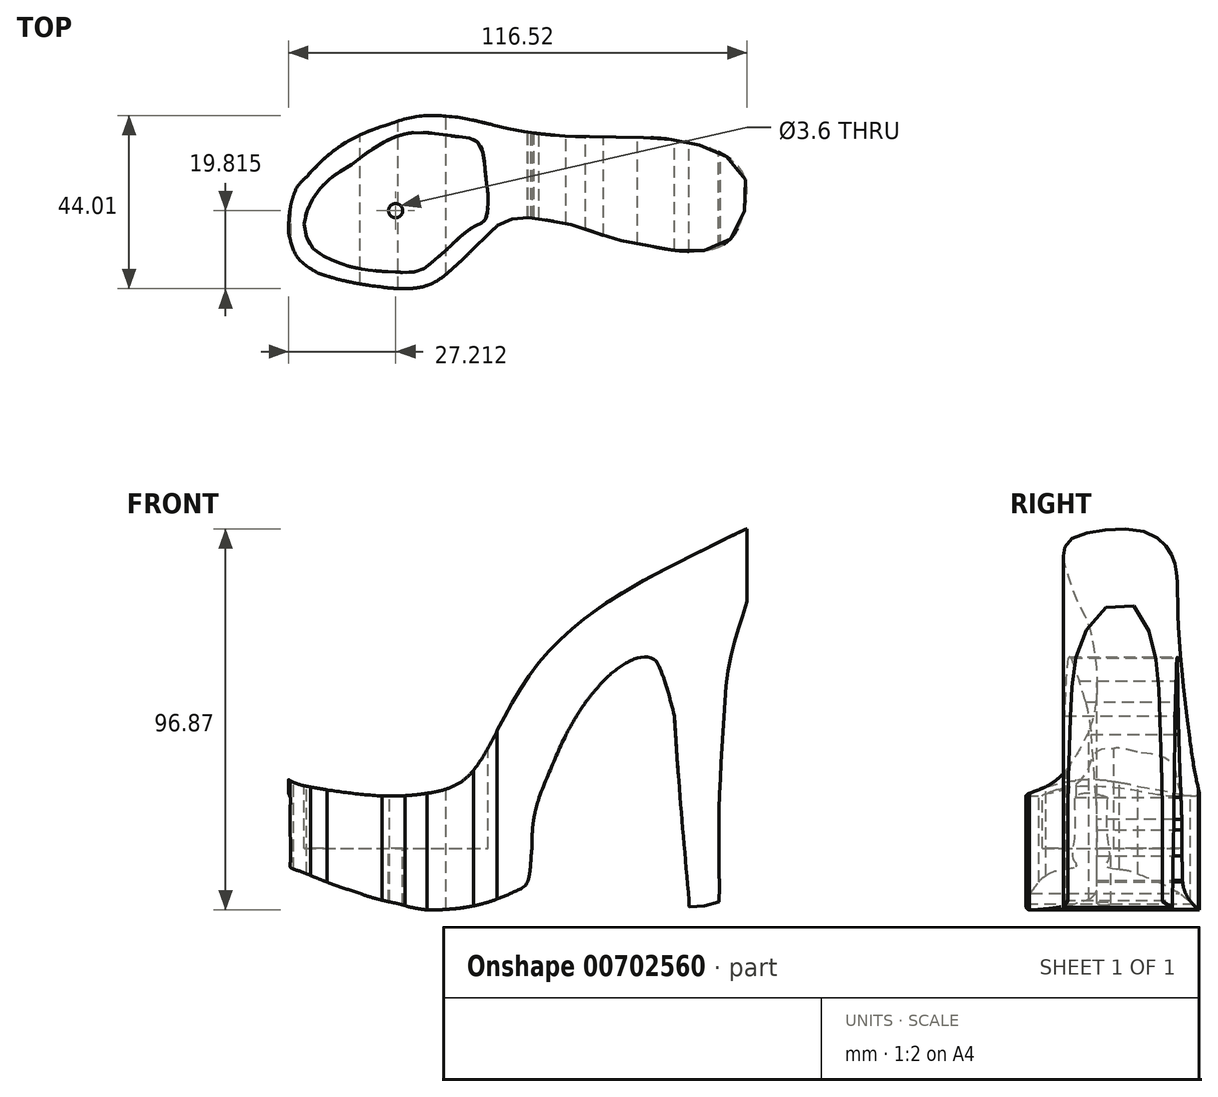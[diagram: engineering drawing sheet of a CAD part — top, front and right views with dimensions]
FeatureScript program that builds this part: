
annotation { "Feature Type Name" : "Feature", "Feature Type Description" : "" }
export const myFeature = defineFeature(function(context is Context, id is Id, definition is map)
    precondition{}
    {
        {
            var Q0;
            Q0=qCreatedBy(makeId("Front.planeOp"),FACE);
            var sketch = newSketch(context, id + "F0", { "sketchPlane" : qUnion([Q0])});
            skFitSpline(sketch, "E0", {"points": [v(-57.93, -19.47) * mm, v(-55.3, -20.89) * mm, v(-50.02, -22.51) * mm, v(-39.07, -24.13) * mm, v(-27.3, -24.74) * mm, v(-16.76, -23.32) * mm, v(-13.11, -21.9) * mm, v(-9.87, -19.47) * mm, v(-6.01, -14.2) * mm, v(-3.78, -10.14) * mm, v(1.7, 0) * mm, v(7.57, 8.72) * mm, v(18.12, 19.27) * mm, v(34.14, 29.81) * mm, v(49.96, 37.93) * mm, v(63.55, 44.21) * mm, v(66.6, 44.42) * mm, v(64.97, 39.75) * mm, v(61.93, 28.6) * mm, v(56.66, 11.15) * mm, v(54.83, -4.66) * mm, v(53.61, -29.2) * mm, v(53.82, -48.27) * mm, v(53.61, -51.51) * mm, v(51.38, -52.53) * mm, v(47.33, -52.93) * mm, v(46.1, -52.93) * mm, v(46.1, -49.69) * mm, v(46.1, -43.4) * mm, v(45.3, -26.97) * mm, v(44.28, -15.62) * mm, v(42.26, -4.46) * mm, v(38.2, 8.52) * mm, v(36.37, 10.34) * mm, v(32.93, 10.34) * mm, v(28.26, 8.52) * mm, v(24.2, 4.46) * mm, v(17.3, -4.46) * mm, v(10, -19.88) * mm, v(6.36, -31.84) * mm, v(4.94, -46.65) * mm, v(2.5, -48.68) * mm, v(-3.17, -51.1) * mm, v(-15.75, -53.54) * mm, v(-27.92, -52.12) * mm, v(-37.65, -49.49) * mm, v(-45.56, -45.23) * mm, v(-51.24, -41.17) * mm, v(-53.07, -35.7) * mm, v(-55.3, -25.15) * mm, v(-57.93, -19.47) * mm]});
            skFitSpline(sketch, "E1", {"points": [v(-55.3, -20.89) * mm, v(-55.3, -25.15) * mm, v(-55.3, -35.7) * mm, v(-55.3, -41.53) * mm, v(-55.3, -42.87) * mm, v(-53.07, -43.82) * mm, v(-49.74, -45.16) * mm, v(-37.65, -49.49) * mm, v(-27.92, -52.12) * mm, v(-15.75, -53.54) * mm, v(4.94, -46.65) * mm, v(4.94, -45.23) * mm, v(5.86, -40.03) * mm, v(6.2, -33.38) * mm, v(7.91, -25.15) * mm, v(14.75, -9.15) * mm, v(24.2, 4.46) * mm, v(32.93, 10.34) * mm, v(38.2, 10.34) * mm, v(41.15, 6.2) * mm, v(42.26, -4.46) * mm, v(46.1, -52.93) * mm], "startDerivative": vector(0.48, -111.33) * mm, "endDerivative": vector(44.54, -510.04) * mm});
            skSolve(sketch);
        }
        {
            var Q0;
            Q0 = qSketchRegion(id + "F0", true);
            extrude(context, id + "F1", {"entities" : qUnion([Q0]), "endBound" : BoundingType.SYMMETRIC, "depth" : 50.8 * mm, "offsetDistance" : 25.4 * mm});
        }
        {
            var Q0;
            Q0=qCreatedBy(makeId("Top.planeOp"),FACE);
            var sketch = newSketch(context, id + "F2", { "sketchPlane" : qUnion([Q0])});
            skFitSpline(sketch, "E2", {"points": [v(-54.46, -12.17) * mm, v(-55.47, -10.75) * mm, v(-55.67, -6.29) * mm, v(-54.46, 0) * mm, v(-51.21, 4.66) * mm, v(-43.1, 12.17) * mm, v(-30.12, 18.05) * mm, v(-15.72, 20.08) * mm, v(-3.75, 17.85) * mm, v(8.21, 15.62) * mm, v(24.24, 14.8) * mm, v(39.65, 14.4) * mm, v(52.22, 11.56) * mm, v(59.12, 6.5) * mm, v(60.74, 0) * mm, v(58.71, -7.7) * mm, v(54.25, -12.78) * mm, v(44.72, -14.2) * mm, v(35.4, -12.78) * mm, v(26.47, -10.95) * mm, v(17.75, -7.9) * mm, v(10.85, -6.5) * mm, v(3.55, -5.68) * mm, v(-2.74, -7.7) * mm, v(-8.82, -13.59) * mm, v(-14.1, -18.66) * mm, v(-20.59, -22.92) * mm, v(-31.94, -23.32) * mm, v(-42.08, -21.3) * mm, v(-50.6, -18.25) * mm, v(-54.46, -12.17) * mm]});
            skLineSegment(sketch, "E3.bottom", {"start": v(-58.72, 26.07) * mm, "end": v(67.31, 26.07) * mm});
            skLineSegment(sketch, "E3.top", {"start": v(-58.72, -26.26) * mm, "end": v(67.31, -26.26) * mm});
            skLineSegment(sketch, "E3.left", {"start": v(-58.72, 26.07) * mm, "end": v(-58.72, -26.26) * mm});
            skLineSegment(sketch, "E3.right", {"start": v(67.31, 26.07) * mm, "end": v(67.31, -26.26) * mm});
            skFitSpline(sketch, "E4", {"points": [v(-2.74, -7.7) * mm, v(-8.82, -13.59) * mm, v(-14.1, -18.66) * mm, v(-20.59, -22.92) * mm, v(-31.94, -23.32) * mm, v(-50.12, -18.66) * mm, v(-55.35, -11.06) * mm, v(-54.46, 0) * mm, v(-51.21, 4.66) * mm, v(-30.12, 18.05) * mm, v(-15.72, 20.08) * mm, v(-3.75, 17.85) * mm], "startDerivative": vector(-79.74, -76.49) * mm, "endDerivative": vector(127.32, -29.11) * mm});
            skSolve(sketch);
        }
        {
            var Q0;
            Q0 = qSketchRegion(id + "F2", true);
            extrude(context, id + "F3", {"entities" : qUnion([Q0]), "operationType" : NewBodyOperationType.REMOVE, "endBound" : BoundingType.SYMMETRIC, "oppositeDirection" : true, "depth" : 127 * mm, "offsetDistance" : 25.4 * mm});
        }
        {
            var Q0;
            Q0=qCreatedBy(makeId("Top.planeOp"),FACE);
            var sketch = newSketch(context, id + "F4", { "sketchPlane" : qUnion([Q0])});
            skFitSpline(sketch, "E5", {"points": [v(-46.27, 3.3) * mm, v(-40.75, 7.22) * mm, v(-31.93, 13.3) * mm, v(-22.95, 15.98) * mm, v(-13.5, 14.98) * mm, v(-7.43, 13.23) * mm, v(-5.64, 4.55) * mm, v(-5.61, -3.12) * mm, v(-12.03, -7.96) * mm, v(-18.45, -12.8) * mm, v(-22.52, -16.22) * mm, v(-30.24, -17.87) * mm, v(-39.14, -17.29) * mm, v(-46.84, -15.5) * mm, v(-50.32, -12.45) * mm, v(-51.6, -5.81) * mm, v(-46.27, 3.3) * mm]});
            skFitSpline(sketch, "E6", {"points": [v(-46.84, -15.5) * mm, v(-41.19, -17.8) * mm, v(-33.8, -19.16) * mm, v(-25.29, -19.56) * mm, v(-21.92, -18.92) * mm, v(-18.95, -16.75) * mm, v(-14.77, -13.05) * mm, v(-12.36, -10.73) * mm, v(-7.95, -7.6) * mm, v(-5.62, -5.9) * mm, v(-5.64, 4.55) * mm], "startDerivative": vector(51.87, -23.9) * mm, "endDerivative": vector(-9.83, 94.1) * mm});
            skSolve(sketch);
        }
        {
            var Q0;
            Q0 = qSketchRegion(id + "F4", true);
            extrude(context, id + "F5", {"entities" : qUnion([Q0]), "operationType" : NewBodyOperationType.REMOVE, "oppositeDirection" : true, "depth" : 38.1 * mm, "offsetDistance" : 25.4 * mm});
        }
        {
            var Q0;
            Q0=makeQuery(id+"F5.boolean.opBoolean","COPY",FACE,{"derivedFrom":makeQuery(id+"F5.opExtrude","CAP_FACE",FACE,{"disambiguationData":[OSD([sQuery(id+"F4.wireOp",EDGE,"E5"),sQuery(id+"F4.wireOp",EDGE,"E6")])],"isStart":false})});
            var sketch = newSketch(context, id + "F6", { "sketchPlane" : qUnion([Q0])});
            skCircle(sketch, "E7", {"center": v(-28.55, -3.91) * mm, "radius": 1.8 * mm});
            skSolve(sketch);
        }
        {
            var Q0;
            Q0 = qSketchRegion(id + "F6", true);
            extrude(context, id + "F7", {"entities" : qUnion([Q0]), "operationType" : NewBodyOperationType.REMOVE, "oppositeDirection" : true, "depth" : 25.4 * mm, "offsetDistance" : 25.4 * mm});
        }
    });
